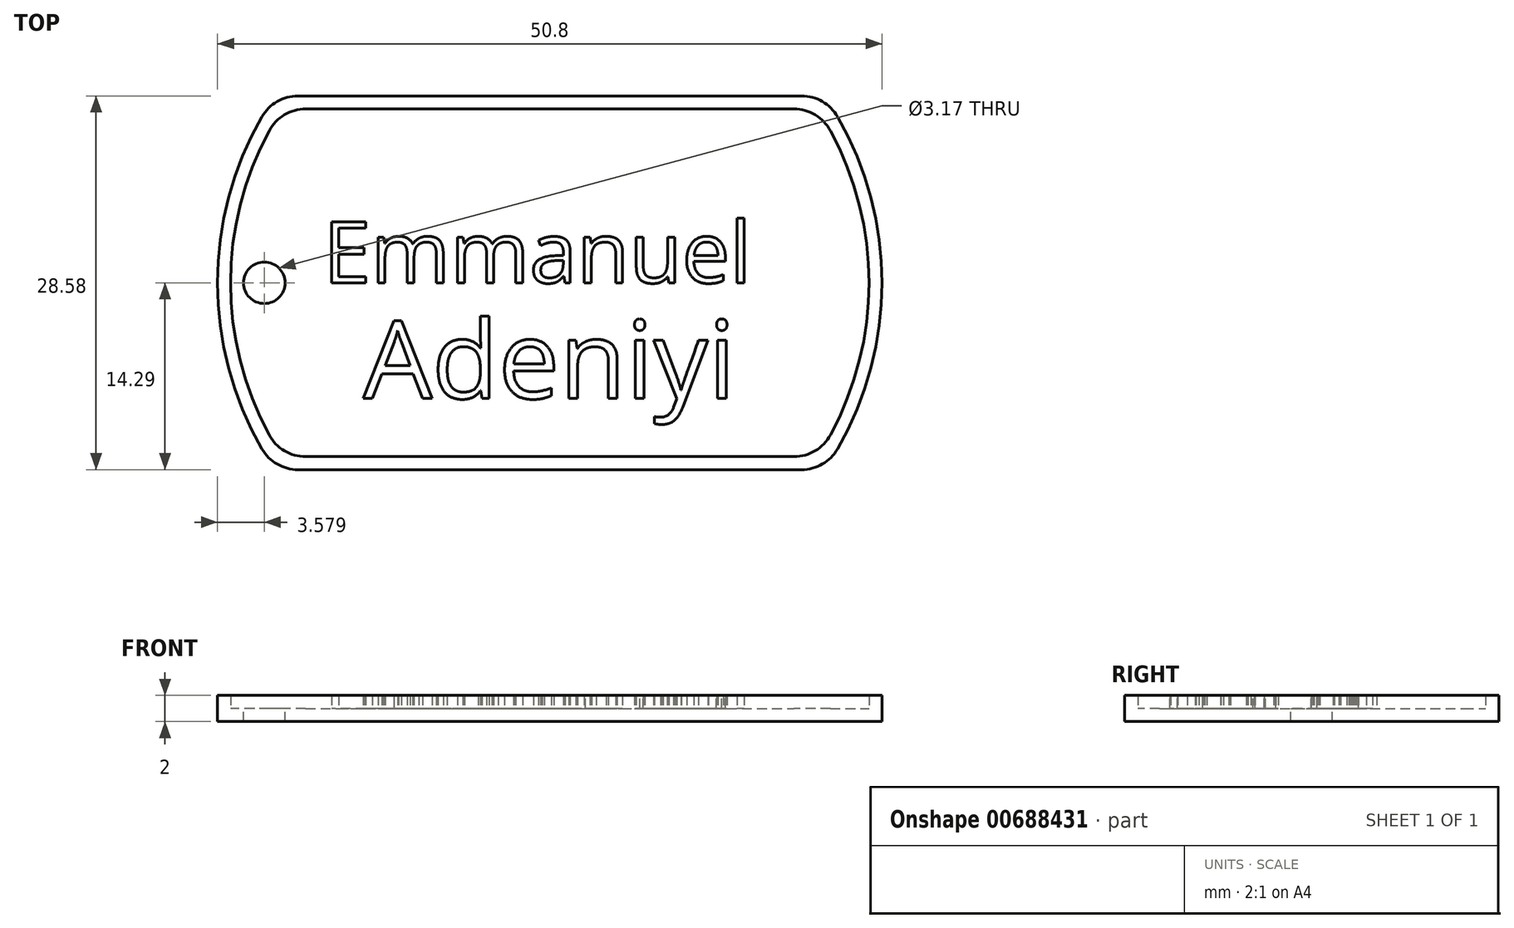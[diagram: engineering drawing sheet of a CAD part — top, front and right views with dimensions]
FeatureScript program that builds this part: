
annotation { "Feature Type Name" : "Feature", "Feature Type Description" : "" }
export const myFeature = defineFeature(function(context is Context, id is Id, definition is map)
    precondition{}
    {
        {
            var Q0;
            Q0=qCreatedBy(makeId("Top.planeOp"),FACE);
            var sketch = newSketch(context, id + "F0", { "sketchPlane" : qUnion([Q0])});
            skArc(sketch, "E0", {"start": v(-22, 12.7) * mm, "mid": v(-25.4, 0) * mm, "end": v(-22, -12.7) * mm});
            skLineSegment(sketch, "E1.top", {"start": v(-19.25, -14.29) * mm, "end": v(19.25, -14.29) * mm});
            skArc(sketch, "E2.trimOffspring", {"start": v(22, -12.7) * mm, "mid": v(25.4, 0) * mm, "end": v(22, 12.7) * mm});
            skLineSegment(sketch, "E3", {"start": v(-19.25, 14.29) * mm, "end": v(19.25, 14.29) * mm});
            skPoint(sketch, "E4.visualSharp", {"position": v(-21, 14.29) * mm});
            skArc(sketch, "E4.filletArc", {"start": v(-19.25, 14.29) * mm, "mid": v(-20.83, 13.86) * mm, "end": v(-22, 12.7) * mm});
            skPoint(sketch, "E5.visualSharp", {"position": v(21, 14.29) * mm});
            skArc(sketch, "E5.filletArc", {"start": v(22, 12.7) * mm, "mid": v(20.83, 13.86) * mm, "end": v(19.25, 14.29) * mm});
            skPoint(sketch, "E6.visualSharp", {"position": v(21, -14.29) * mm});
            skArc(sketch, "E6.filletArc", {"start": v(19.25, -14.29) * mm, "mid": v(20.83, -13.86) * mm, "end": v(22, -12.7) * mm});
            skPoint(sketch, "E7.visualSharp", {"position": v(-21, -14.29) * mm});
            skArc(sketch, "E7.filletArc", {"start": v(-22, -12.7) * mm, "mid": v(-20.83, -13.86) * mm, "end": v(-19.25, -14.29) * mm});
            skSolve(sketch);
        }
        {
            var Q0;
            Q0=makeQuery(id+"F0.imprint","IMPRINT",FACE,{"disambiguationData":[TD([[makeQuery(id+"F0.imprint","IMPRINT",EDGE,{"derivedFrom":sQuery(id+"F0.wireOp",EDGE,"E0")}),1.0]])]});
            extrude(context, id + "F1", {"entities" : qUnion([Q0]), "depth" : 1 * mm, "offsetDistance" : 25.4 * mm});
        }
        {
            var Q0;
            Q0=makeQuery(id+"F1.opExtrude","CAP_FACE",FACE,{"disambiguationData":[OSD([sQuery(id+"F0.wireOp",EDGE,"E0"),sQuery(id+"F0.wireOp",EDGE,"E1.top"),sQuery(id+"F0.wireOp",EDGE,"E2.trimOffspring"),sQuery(id+"F0.wireOp",EDGE,"E3"),sQuery(id+"F0.wireOp",EDGE,"E4.filletArc"),sQuery(id+"F0.wireOp",EDGE,"E5.filletArc"),sQuery(id+"F0.wireOp",EDGE,"E6.filletArc"),sQuery(id+"F0.wireOp",EDGE,"E7.filletArc")])],"isStart":false});
            var sketch = newSketch(context, id + "F2", { "sketchPlane" : qUnion([Q0])});
            skLineSegment(sketch, "E8.0", {"start": v(-18.66, 13.29) * mm, "end": v(18.66, 13.29) * mm});
            skArc(sketch, "E8.1", {"start": v(-21.45, 11.63) * mm, "mid": v(-24.4, 0) * mm, "end": v(-21.45, -11.63) * mm});
            skLineSegment(sketch, "E8.2", {"start": v(-18.66, -13.29) * mm, "end": v(18.66, -13.29) * mm});
            skArc(sketch, "E8.3", {"start": v(21.45, -11.63) * mm, "mid": v(24.4, 0) * mm, "end": v(21.45, 11.63) * mm});
            skPoint(sketch, "E9.visualSharp", {"position": v(-20.46, 13.29) * mm});
            skArc(sketch, "E9.filletArc", {"start": v(-18.66, 13.29) * mm, "mid": v(-20.29, 12.84) * mm, "end": v(-21.45, 11.63) * mm});
            skPoint(sketch, "E10.visualSharp", {"position": v(20.46, 13.29) * mm});
            skArc(sketch, "E10.filletArc", {"start": v(21.45, 11.63) * mm, "mid": v(20.29, 12.84) * mm, "end": v(18.66, 13.29) * mm});
            skPoint(sketch, "E11.visualSharp", {"position": v(20.46, -13.29) * mm});
            skArc(sketch, "E11.filletArc", {"start": v(18.66, -13.29) * mm, "mid": v(20.29, -12.84) * mm, "end": v(21.45, -11.63) * mm});
            skPoint(sketch, "E12.visualSharp", {"position": v(-20.46, -13.29) * mm});
            skArc(sketch, "E12.filletArc", {"start": v(-21.45, -11.63) * mm, "mid": v(-20.29, -12.84) * mm, "end": v(-18.66, -13.29) * mm});
            skLineSegment(sketch, "E13.0", {"start": v(-19.25, 14.29) * mm, "end": v(19.25, 14.29) * mm});
            skArc(sketch, "E13.1", {"start": v(-22, 12.7) * mm, "mid": v(-25.4, 0) * mm, "end": v(-22, -12.7) * mm});
            skLineSegment(sketch, "E13.2", {"start": v(-19.25, -14.29) * mm, "end": v(19.25, -14.29) * mm});
            skArc(sketch, "E13.3", {"start": v(22, -12.7) * mm, "mid": v(25.4, 0) * mm, "end": v(22, 12.7) * mm});
            skPoint(sketch, "E14.visualSharp", {"position": v(-21, -14.29) * mm});
            skArc(sketch, "E14.filletArc", {"start": v(-22, -12.7) * mm, "mid": v(-20.83, -13.86) * mm, "end": v(-19.25, -14.29) * mm});
            skPoint(sketch, "E15.visualSharp", {"position": v(21, -14.29) * mm});
            skArc(sketch, "E15.filletArc", {"start": v(19.25, -14.29) * mm, "mid": v(20.83, -13.86) * mm, "end": v(22, -12.7) * mm});
            skPoint(sketch, "E16.visualSharp", {"position": v(21, 14.29) * mm});
            skArc(sketch, "E16.filletArc", {"start": v(22, 12.7) * mm, "mid": v(20.83, 13.86) * mm, "end": v(19.25, 14.29) * mm});
            skPoint(sketch, "E17.visualSharp", {"position": v(-21, 14.29) * mm});
            skArc(sketch, "E17.filletArc", {"start": v(-19.25, 14.29) * mm, "mid": v(-20.83, 13.86) * mm, "end": v(-22, 12.7) * mm});
            skSolve(sketch);
        }
        {
            var Q0;
            Q0=makeQuery(id+"F2.imprint","IMPRINT",FACE,{"disambiguationData":[TD([[makeQuery(id+"F2.imprint","IMPRINT",EDGE,{"derivedFrom":sQuery(id+"F2.wireOp",EDGE,"E8.0")}),1.0]])]});
            extrude(context, id + "F3", {"entities" : qUnion([Q0]), "operationType" : NewBodyOperationType.ADD, "depth" : 1 * mm, "offsetDistance" : 25.4 * mm});
        }
        {
            var Q0;
            Q0=makeQuery(id+"F1.opExtrude","CAP_FACE",FACE,{"disambiguationData":[OSD([sQuery(id+"F0.wireOp",EDGE,"E0"),sQuery(id+"F0.wireOp",EDGE,"E1.top"),sQuery(id+"F0.wireOp",EDGE,"E2.trimOffspring"),sQuery(id+"F0.wireOp",EDGE,"E3"),sQuery(id+"F0.wireOp",EDGE,"E4.filletArc"),sQuery(id+"F0.wireOp",EDGE,"E5.filletArc"),sQuery(id+"F0.wireOp",EDGE,"E6.filletArc"),sQuery(id+"F0.wireOp",EDGE,"E7.filletArc")])],"isStart":false});
            var sketch = newSketch(context, id + "F4", { "sketchPlane" : qUnion([Q0])});
            skCircle(sketch, "E18", {"center": v(-21.82, 0) * mm, "radius": 1.59 * mm});
            skSolve(sketch);
        }
        {
            var Q0;
            Q0=makeQuery(id+"F4.imprint","IMPRINT",FACE,{"disambiguationData":[TD([[makeQuery(id+"F4.imprint","IMPRINT",EDGE,{"derivedFrom":sQuery(id+"F4.wireOp",EDGE,"E18")}),1.0]])]});
            extrude(context, id + "F5", {"entities" : qUnion([Q0]), "operationType" : NewBodyOperationType.REMOVE, "oppositeDirection" : true, "depth" : 1 * mm, "offsetDistance" : 25.4 * mm});
        }
        {
            var Q0;
            Q0=makeQuery(id+"F2.imprint","IMPRINT",FACE,{"disambiguationData":[TD([[makeQuery(id+"F2.imprint","IMPRINT",EDGE,{"derivedFrom":sQuery(id+"F2.wireOp",EDGE,"E8.0")}),-1.0]])]});
            var sketch = newSketch(context, id + "F6", { "sketchPlane" : qUnion([Q0])});
            skText(sketch, "E19", { "text": "Emmanuel", "fontName": "OpenSans-Regular.ttf"});
            const initialGuessF6  = {"E19": [-0.01732, 0, 1, 0, 0.0047]};
            skSetInitialGuess(sketch, initialGuessF6);
            skSolve(sketch);
        }
        {
            var Q0;
            Q0=makeQuery(id+"F2.imprint","IMPRINT",FACE,{"disambiguationData":[TD([[makeQuery(id+"F2.imprint","IMPRINT",EDGE,{"derivedFrom":sQuery(id+"F2.wireOp",EDGE,"E8.0")}),-1.0]])]});
            var sketch = newSketch(context, id + "F7", { "sketchPlane" : qUnion([Q0])});
            skText(sketch, "E20", { "text": "Adeniyi", "fontName": "OpenSans-Regular.ttf"});
            const initialGuessF7  = {"E20": [-0.01425, -0.00884, 1, 0, 0.00597]};
            skSetInitialGuess(sketch, initialGuessF7);
            skSolve(sketch);
        }
        {
            var Q0;
            Q0 = qSketchRegion(id + "F7", true);
            var Q1;
            Q1 = qSketchRegion(id + "F6", true);
            extrude(context, id + "F8", {"entities" : qUnion([Q0, Q1]), "operationType" : NewBodyOperationType.ADD, "depth" : 1 * mm, "offsetDistance" : 25.4 * mm});
        }
    });
